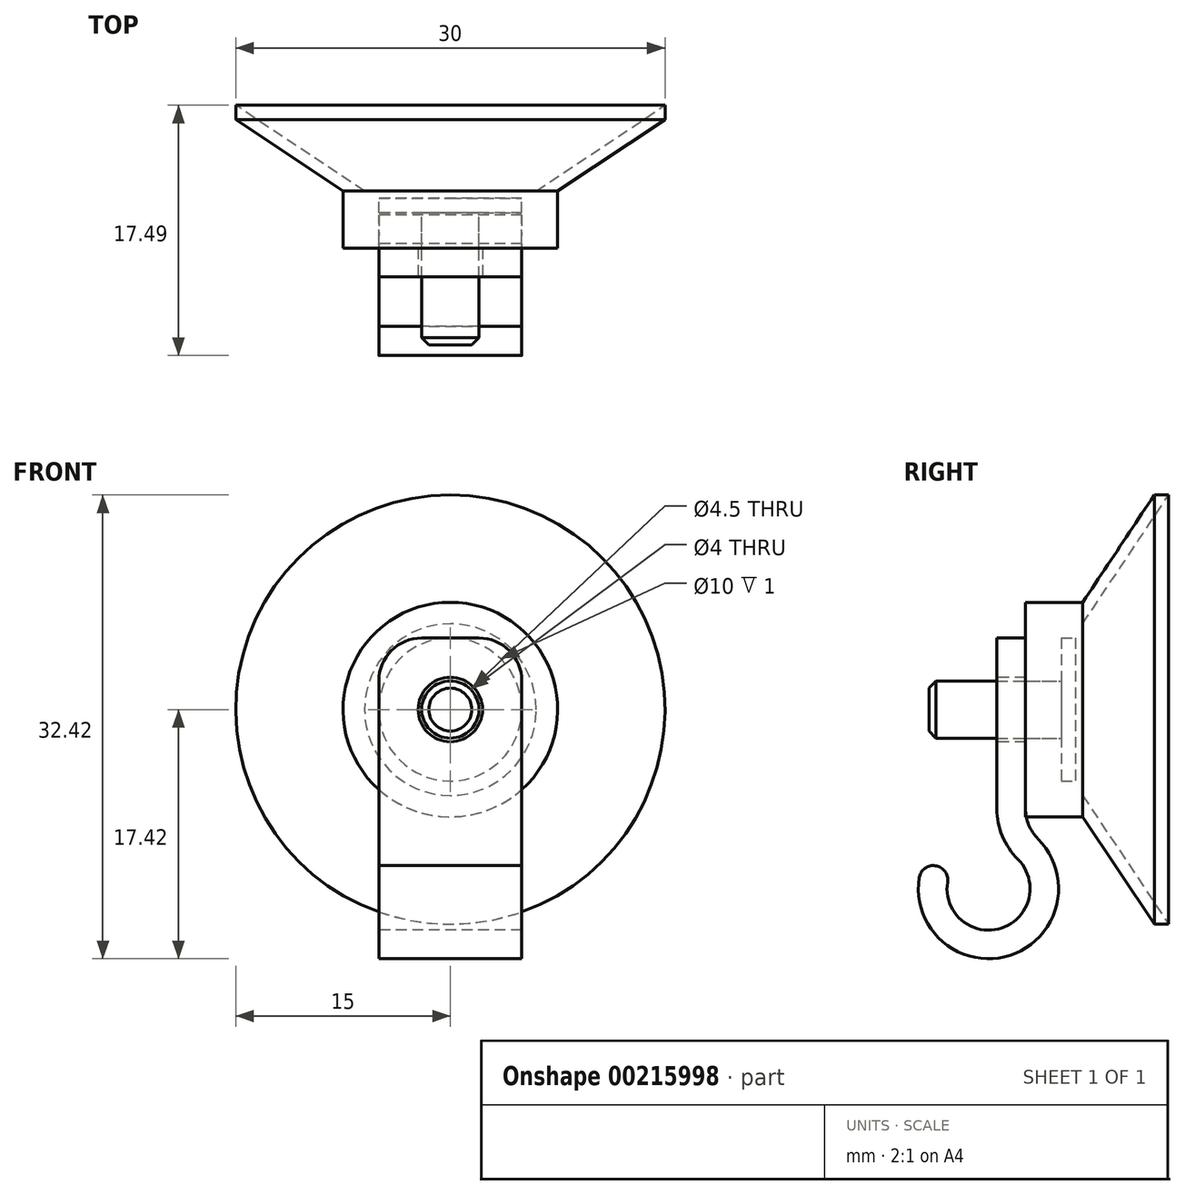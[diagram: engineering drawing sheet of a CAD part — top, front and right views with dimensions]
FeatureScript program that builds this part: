
annotation { "Feature Type Name" : "Feature", "Feature Type Description" : "" }
export const myFeature = defineFeature(function(context is Context, id is Id, definition is map)
    precondition{}
    {
        {
            var Q0;
            Q0=qCreatedBy(makeId("Right.planeOp"),FACE);
            var sketch = newSketch(context, id + "F0", { "sketchPlane" : qUnion([Q0])});
            skLineSegment(sketch, "E0.bottom", {"start": v(0, 0) * mm, "end": v(4, 0) * mm});
            skLineSegment(sketch, "E0.top", {"start": v(0, 7.5) * mm, "end": v(4, 7.5) * mm});
            skLineSegment(sketch, "E0.left", {"start": v(0, 2) * mm, "end": v(0, 7.5) * mm});
            skLineSegment(sketch, "E0.right", {"start": v(4, 0) * mm, "end": v(4, 6) * mm});
            skLineSegment(sketch, "E1", {"start": v(4, 7.5) * mm, "end": v(9, 15) * mm});
            skLineSegment(sketch, "E2", {"start": v(10, 15) * mm, "end": v(4, 6) * mm});
            skLineSegment(sketch, "E3", {"start": v(10, 15) * mm, "end": v(9, 15) * mm});
            skLineSegment(sketch, "E4", {"start": v(0, 0) * mm, "end": v(-6.75, 0) * mm});
            skLineSegment(sketch, "E5", {"start": v(-6.75, 0) * mm, "end": v(-6.75, 2) * mm});
            skLineSegment(sketch, "E6", {"start": v(-6.75, 2) * mm, "end": v(0, 2) * mm});
            skLineSegment(sketch, "E7", {"start": v(0, 2) * mm, "end": v(2.5, 2) * mm});
            skLineSegment(sketch, "E8", {"start": v(2.5, 2) * mm, "end": v(2.5, 5) * mm});
            skLineSegment(sketch, "E9", {"start": v(2.5, 5) * mm, "end": v(3.5, 5) * mm});
            skLineSegment(sketch, "E10", {"start": v(3.5, 5) * mm, "end": v(3.5, 0) * mm});
            skSolve(sketch);
        }
        {
            var Q0;
            Q0=makeQuery(id+"F0.imprint","IMPRINT",FACE,{"disambiguationData":[TD([[makeQuery(id+"F0.imprint","IMPRINT",EDGE,{"derivedFrom":sQuery(id+"F0.wireOp",EDGE,"E0.top")}),-1.0]])]});
            var Q1;
            Q1=sQuery(id+"F0.wireOp",EDGE,"E4");
            revolve(context, id + "F1", {"entities" : qUnion([Q0]), "axis" : qUnion([Q1]), "revolveType" : RevolveType.FULL});
        }
        {
            var Q0;
            {var subQ0=sQuery(id+"F0.wireOp",EDGE,"E4");Q0=makeQuery(id+"F0.imprint","IMPRINT",FACE,{"disambiguationData":[TD([[makeQuery(id+"F0.imprint","IMPRINT",EDGE,{"derivedFrom":subQ0}),-1.0]])]});}
            var Q1;
            Q1=sQuery(id+"F0.wireOp",EDGE,"E4");
            revolve(context, id + "F2", {"entities" : qUnion([Q0]), "axis" : qUnion([Q1]), "revolveType" : RevolveType.FULL});
        }
        {
            var Q0;
            Q0=makeQuery(id+"F2.opRevolve","SWEPT_EDGE",EDGE,{"disambiguationData":[OSD([sQuery(id+"F0.wireOp",EDGE,"E5"),sQuery(id+"F0.wireOp",EDGE,"E6")])]});
            chamfer(context, id + "F3", {"entities" : qUnion([Q0]), "width" : .5 * mm, "tangentPropagation" : true});
        }
        {
            var Q0;
            Q0=qCreatedBy(makeId("Right.planeOp"),FACE);
            var sketch = newSketch(context, id + "F4", { "sketchPlane" : qUnion([Q0])});
            skLineSegment(sketch, "E11", {"start": v(-2, 5) * mm, "end": v(-2, -6.93) * mm});
            skLineSegment(sketch, "E12", {"start": v(-0.54, -10.46) * mm, "end": v(5.64, -16.64) * mm, "construction": true});
            skPoint(sketch, "E13.visualSharp", {"position": v(-2, -9) * mm});
            skArc(sketch, "E13.filletArc", {"start": v(-2, -6.93) * mm, "mid": v(-1.62, -8.84) * mm, "end": v(-0.54, -10.46) * mm});
            skArc(sketch, "E14", {"start": v(-5.45, -12.06) * mm, "mid": v(-1.69, -15.27) * mm, "end": v(-0.54, -10.46) * mm});
            skLineSegment(sketch, "E15", {"start": v(-7.45, -17.38) * mm, "end": v(3, -6.93) * mm, "construction": true});
            skLineSegment(sketch, "E16", {"start": v(-2.59, -12.52) * mm, "end": v(-9.65, -11.4) * mm, "construction": true});
            skArc(sketch, "E17.0", {"start": v(-7.43, -11.75) * mm, "mid": v(-1.07, -17.18) * mm, "end": v(0.88, -9.05) * mm});
            skArc(sketch, "E17.1", {"start": v(0, -6.93) * mm, "mid": v(0.23, -8.08) * mm, "end": v(0.88, -9.05) * mm});
            skLineSegment(sketch, "E17.2", {"start": v(0, 5) * mm, "end": v(0, -6.93) * mm});
            skLineSegment(sketch, "E18", {"start": v(0, 5) * mm, "end": v(-2, 5) * mm});
            skArc(sketch, "E19", {"start": v(-5.45, -12.06) * mm, "mid": v(-6.28, -10.92) * mm, "end": v(-7.43, -11.75) * mm});
            skSolve(sketch);
        }
        {
            var Q0;
            Q0 = qSketchRegion(id + "F4", true);
            extrude(context, id + "F5", {"entities" : qUnion([Q0]), "endBound" : BoundingType.SYMMETRIC, "depth" : 10 * mm});
        }
        {
            var Q0;
            Q0=makeQuery(id+"F5.opExtrude","CAP_EDGE",EDGE,{"disambiguationData":[OSD([sQuery(id+"F4.wireOp",EDGE,"E18")])],"isStart":true});
            var Q1;
            Q1=makeQuery(id+"F5.opExtrude","CAP_EDGE",EDGE,{"disambiguationData":[OSD([sQuery(id+"F4.wireOp",EDGE,"E18")])],"isStart":false});
            fillet(context, id + "F6", {"entities" : qUnion([Q0, Q1]), "radius" : 3 * mm, "tangentPropagation" : true, "allowEdgeOverflow" : false});
        }
        {
            var Q0;
            Q0=makeQuery(id+"F5.opExtrude","SWEPT_FACE",FACE,{"disambiguationData":[OSD([sQuery(id+"F4.wireOp",EDGE,"E11")])]});
            var sketch = newSketch(context, id + "F7", { "sketchPlane" : qUnion([Q0])});
            skPoint(sketch, "E20", {"position": v(0, 0) * mm});
            skSolve(sketch);
        }
        {
            var Q0;
            Q0=sQuery(id+"F7.wireOp",VERTEX,"E20");
            var Q1;
            Q1=makeQuery(id+"F5.opExtrude","SWEPT_BODY",BODY,{"disambiguationData":[OSD([sQuery(id+"F4.wireOp",EDGE,"E11"),sQuery(id+"F4.wireOp",EDGE,"E13.filletArc"),sQuery(id+"F4.wireOp",EDGE,"E14"),sQuery(id+"F4.wireOp",EDGE,"E17.0"),sQuery(id+"F4.wireOp",EDGE,"E17.1"),sQuery(id+"F4.wireOp",EDGE,"E17.2"),sQuery(id+"F4.wireOp",EDGE,"E18"),sQuery(id+"F4.wireOp",EDGE,"1d183dff-f9e8-427c-809c-e922a8f7f4ba")])]});
            hole(context, id + "F8", {"style" : HoleStyle.SIMPLE, "endStyle" : HoleEndStyle.THROUGH, "holeDiameter" : 4.5 * mm, "startFromSketch" : true, "locations" : qUnion([Q0]), "scope" : qUnion([Q1]), "isTappedThrough" : true});
        }
    });
